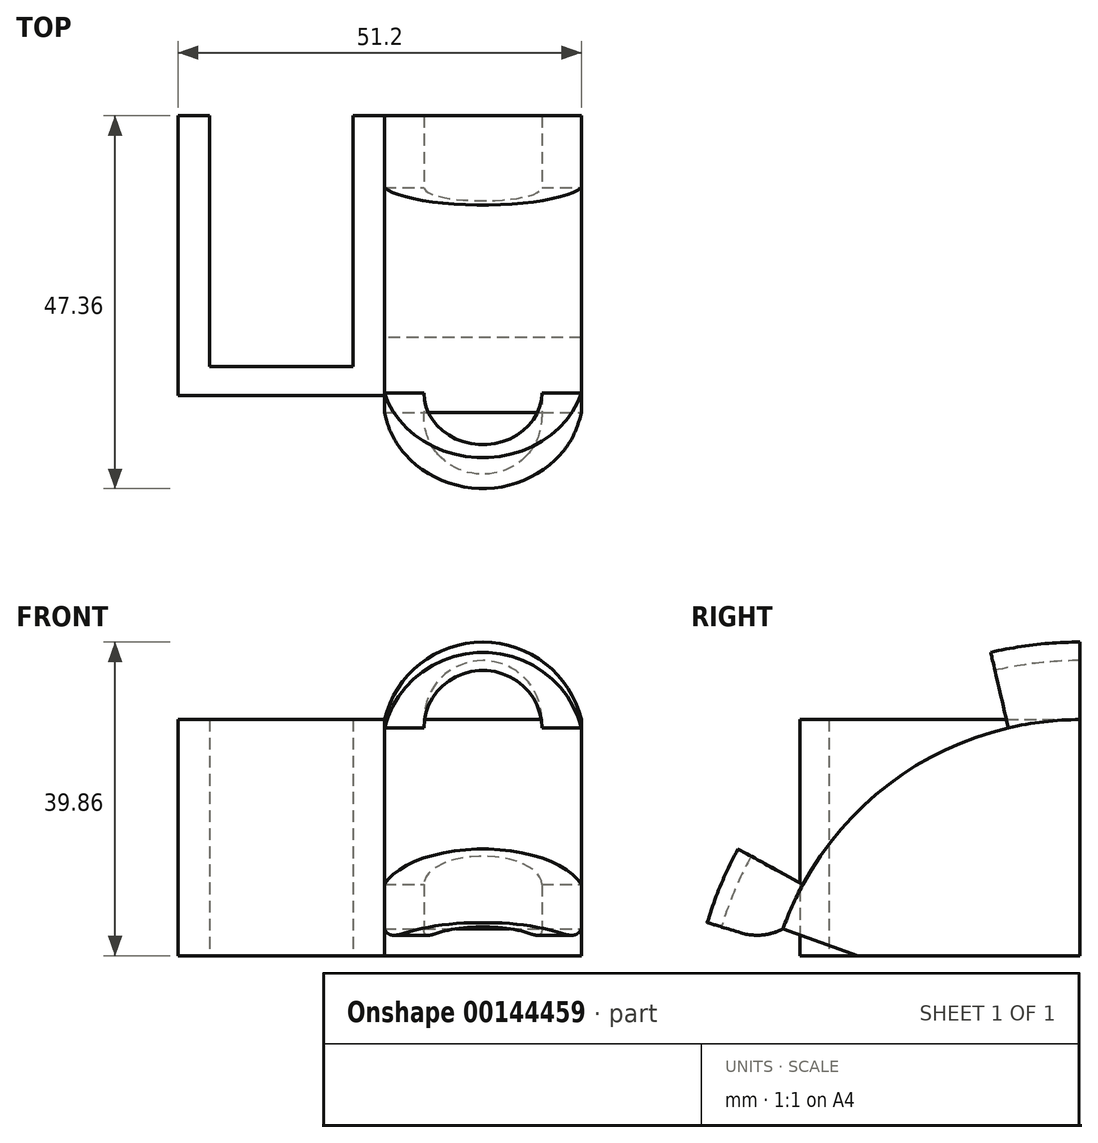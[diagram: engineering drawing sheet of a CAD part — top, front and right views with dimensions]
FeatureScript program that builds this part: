
annotation { "Feature Type Name" : "Feature", "Feature Type Description" : "" }
export const myFeature = defineFeature(function(context is Context, id is Id, definition is map)
    precondition{}
    {
        {
            var Q0;
            Q0=qCreatedBy(makeId("Top.planeOp"),FACE);
            var sketch = newSketch(context, id + "F0", { "sketchPlane" : qUnion([Q0])});
            skLineSegment(sketch, "E0.bottom", {"start": v(0, 0) * mm, "end": v(-4, 0) * mm});
            skLineSegment(sketch, "E0.top", {"start": v(0, 35.56) * mm, "end": v(-4, 35.56) * mm});
            skLineSegment(sketch, "E0.left", {"start": v(0, 0) * mm, "end": v(0, 35.56) * mm});
            skLineSegment(sketch, "E0.right", {"start": v(-4, 0) * mm, "end": v(-4, 35.56) * mm});
            skLineSegment(sketch, "E1.bottom", {"start": v(-4, 0) * mm, "end": v(-22.2, 0) * mm});
            skLineSegment(sketch, "E1.top", {"start": v(-4, 3.67) * mm, "end": v(-22.2, 3.67) * mm});
            skLineSegment(sketch, "E1.left", {"start": v(-4, 0) * mm, "end": v(-4, 3.67) * mm});
            skLineSegment(sketch, "E1.right", {"start": v(-22.2, 0) * mm, "end": v(-22.2, 3.67) * mm});
            skLineSegment(sketch, "E2.bottom", {"start": v(-22.2, 0) * mm, "end": v(-26.2, 0) * mm});
            skLineSegment(sketch, "E2.top", {"start": v(-22.2, 35.56) * mm, "end": v(-26.2, 35.56) * mm});
            skLineSegment(sketch, "E2.left", {"start": v(-22.2, 0) * mm, "end": v(-22.2, 35.56) * mm});
            skLineSegment(sketch, "E2.right", {"start": v(-26.2, 0) * mm, "end": v(-26.2, 35.56) * mm});
            skSolve(sketch);
        }
        {
            var Q0;
            Q0 = qSketchRegion(id + "F0", true);
            extrude(context, id + "F1", {"entities" : qUnion([Q0]), "depth" : 30 * mm});
        }
        {
            var Q0;
            Q0=makeQuery(id+"F1.opExtrude","SWEPT_FACE",FACE,{"disambiguationData":[OSD([sQuery(id+"F0.wireOp",EDGE,"E0.left")])]});
            var sketch = newSketch(context, id + "F2", { "sketchPlane" : qUnion([Q0])});
            skArc(sketch, "E3", {"start": v(35.56, 19.88) * mm, "mid": v(18.32, 14.4) * mm, "end": v(7.36, 0) * mm});
            skLineSegment(sketch, "E4", {"start": v(35.56, 0) * mm, "end": v(7.36, 0) * mm});
            skLineSegment(sketch, "E5", {"start": v(35.56, 0) * mm, "end": v(35.56, 19.88) * mm});
            skLineSegment(sketch, "E6", {"start": v(35.56, 30) * mm, "end": v(35.56, -28.36) * mm, "construction": true});
            skPoint(sketch, "E6.endSnap0", {"position": v(35.56, 9.94) * mm});
            skLineSegment(sketch, "E7", {"start": v(35.6, -10.12) * mm, "end": v(0, -10.12) * mm, "construction": true});
            skSolve(sketch);
        }
        {
            var Q0;
            {var subQ0=sQuery(id+"F2.wireOp",EDGE,"E4");Q0=makeQuery(id+"F2.imprint","IMPRINT",FACE,{"disambiguationData":[TD([[makeQuery(id+"F2.imprint","IMPRINT",EDGE,{"derivedFrom":subQ0}),1.0]])]});}
            extrude(context, id + "F3", {"entities" : qUnion([Q0]), "operationType" : NewBodyOperationType.ADD, "depth" : 25 * mm});
        }
        {
            var Q0;
            Q0=makeQuery(id+"F3.boolean.opBoolean","MERGE",FACE,{"derivedFrom":[makeQuery(id+"F1.opExtrude","SWEPT_FACE",FACE,{"disambiguationData":[OSD([sQuery(id+"F0.wireOp",EDGE,"E0.top")])]}),makeQuery(id+"F3.opExtrude","SWEPT_FACE",FACE,{"disambiguationData":[OSD([sQuery(id+"F2.wireOp",EDGE,"E5")])]})]});
            var sketch = newSketch(context, id + "F4", { "sketchPlane" : qUnion([Q0])});
            skLineSegment(sketch, "E8", {"start": v(0, 30) * mm, "end": v(0, 19.88) * mm});
            skLineSegment(sketch, "E9", {"start": v(0, 19.88) * mm, "end": v(-25, 19.88) * mm});
            skLineSegment(sketch, "E10", {"start": v(-25, 19.88) * mm, "end": v(-25, 30) * mm});
            skLineSegment(sketch, "E11", {"start": v(0, 30) * mm, "end": v(-25, 30) * mm});
            skCircle(sketch, "E12", {"center": v(-12.5, 30) * mm, "radius": 7.5 * mm});
            skSolve(sketch);
        }
        {
            var Q0;
            {var subQ0=sQuery(id+"F4.wireOp",EDGE,"E11");var subQ6=sQuery(id+"F4.wireOp",EDGE,"E12");var subQ7=makeQuery(id+"F4.imprint","INTERSECT",VERTEX,{"disambiguationData":[OD(0.0)],"derivedFrom":[subQ0,subQ6]});Q0=makeQuery(id+"F4.imprint","IMPRINT",FACE,{"disambiguationData":[TD([[makeQuery(id+"F4.imprint","IMPRINT",EDGE,{"disambiguationData":[TD([[subQ7,1.0]])],"derivedFrom":subQ0}),1.0]])]});}
            var Q1;
            {var subQ0=sQuery(id+"F4.wireOp",EDGE,"E10");var subQ3=sQuery(id+"F4.wireOp",EDGE,"E11");var subQ4=makeQuery(id+"F4.imprint","INTERSECT",VERTEX,{"derivedFrom":[subQ0,subQ3]});Q1=makeQuery(id+"F4.imprint","IMPRINT",FACE,{"disambiguationData":[TD([[makeQuery(id+"F4.imprint","IMPRINT",EDGE,{"disambiguationData":[TD([[subQ4,1.0]])],"derivedFrom":subQ3}),1.0]])]});}
            var Q2;
            Q2=sQuery(id+"F2.wireOp",EDGE,"E3");
            sweep(context, id + "F5", {"operationType" : NewBodyOperationType.ADD, "profiles" : qUnion([Q0, Q1]), "path" : qUnion([Q2])});
        }
        {
            var Q0;
            {var subQ0=sQuery(id+"F2.wireOp",EDGE,"E5");var subQ1=sQuery(id+"F0.wireOp",EDGE,"E0.top");Q0=makeQuery(id+"F5.boolean.opBoolean","MERGE",FACE,{"derivedFrom":[makeQuery(id+"F3.boolean.opBoolean","MERGE",FACE,{"derivedFrom":[makeQuery(id+"F1.opExtrude","SWEPT_FACE",FACE,{"disambiguationData":[OSD([subQ1])]}),makeQuery(id+"F3.opExtrude","SWEPT_FACE",FACE,{"disambiguationData":[OSD([subQ0])]})]}),makeQuery(id+"F5.opSweep","CAP_FACE",FACE,{"disambiguationData":[OSD([subQ1,sQuery(id+"F0.wireOp",EDGE,"E0.right"),sQuery(id+"F2.wireOp",VERTEX,"E3.start"),sQuery(id+"F2.wireOp",EDGE,"E4"),subQ0,sQuery(id+"F4.wireOp",EDGE,"E10"),sQuery(id+"F4.wireOp",EDGE,"E11"),sQuery(id+"F4.wireOp",EDGE,"E12")])],"isStart":true})]});}
            var sketch = newSketch(context, id + "F6", { "sketchPlane" : qUnion([Q0])});
            skArc(sketch, "E13", {"start": v(-5, 30) * mm, "mid": v(-12.5, 37.5) * mm, "end": v(-20, 30) * mm});
            skArc(sketch, "E14", {"start": v(0, 30) * mm, "mid": v(-12.5, 39.86) * mm, "end": v(-25, 30) * mm});
            skLineSegment(sketch, "E15", {"start": v(-25, 30) * mm, "end": v(-20, 30) * mm});
            skLineSegment(sketch, "E16", {"start": v(-5, 30) * mm, "end": v(0, 30) * mm});
            skSolve(sketch);
        }
        {
            var Q0;
            {var subQ0=sQuery(id+"F2.wireOp",EDGE,"E3");Q0=makeQuery(id+"F5.boolean.opBoolean","MERGE",FACE,{"derivedFrom":[makeQuery(id+"F3.opExtrude","CAP_FACE",FACE,{"disambiguationData":[OSD([subQ0,sQuery(id+"F2.wireOp",EDGE,"E4"),sQuery(id+"F2.wireOp",EDGE,"E5")])],"isStart":false}),makeQuery(id+"F5.opSweep","SWEPT_FACE",FACE,{"disambiguationData":[OSD([subQ0,sQuery(id+"F4.wireOp",EDGE,"E10")])]})]});}
            var sketch = newSketch(context, id + "F7", { "sketchPlane" : qUnion([Q0])});
            skArc(sketch, "E17", {"start": v(35.56, 24.88) * mm, "mid": v(31.56, 24.64) * mm, "end": v(27.62, 23.95) * mm});
            skLineSegment(sketch, "E18", {"start": v(35.6, -10.12) * mm, "end": v(35.56, 24.88) * mm});
            skLineSegment(sketch, "E19", {"start": v(35.6, -10.12) * mm, "end": v(27.62, 23.95) * mm});
            skSolve(sketch);
        }
        {
            var Q0;
            Q0=makeQuery(id+"F6.imprint","IMPRINT",FACE,{"disambiguationData":[TD([[makeQuery(id+"F6.imprint","IMPRINT",EDGE,{"derivedFrom":sQuery(id+"F6.wireOp",EDGE,"E13")}),-1.0]])]});
            var Q1;
            Q1=sQuery(id+"F7.wireOp",EDGE,"E17");
            sweep(context, id + "F8", {"operationType" : NewBodyOperationType.ADD, "profiles" : qUnion([Q0]), "path" : qUnion([Q1])});
        }
        {
            var Q0;
            Q0=makeQuery(id+"F5.opSweep","CAP_FACE",FACE,{"disambiguationData":[OSD([sQuery(id+"F2.wireOp",VERTEX,"E3.end"),sQuery(id+"F4.wireOp",EDGE,"E8"),sQuery(id+"F4.wireOp",EDGE,"E9"),sQuery(id+"F4.wireOp",EDGE,"E10"),sQuery(id+"F4.wireOp",EDGE,"E11"),sQuery(id+"F4.wireOp",EDGE,"E12")])],"isStart":false});
            var sketch = newSketch(context, id + "F9", { "sketchPlane" : qUnion([Q0])});
            skArc(sketch, "E20", {"start": v(20, 3.2) * mm, "mid": v(12.5, 10.7) * mm, "end": v(5, 3.2) * mm});
            skArc(sketch, "E21", {"start": v(25, 3.2) * mm, "mid": v(12.5, 12.6) * mm, "end": v(0, 3.2) * mm});
            skLineSegment(sketch, "E22", {"start": v(0, 3.2) * mm, "end": v(5, 3.2) * mm});
            skLineSegment(sketch, "E23", {"start": v(20, 3.2) * mm, "end": v(25, 3.2) * mm});
            skSolve(sketch);
        }
        {
            var Q0;
            {var subQ0=sQuery(id+"F2.wireOp",EDGE,"E3");Q0=makeQuery(id+"F5.boolean.opBoolean","MERGE",FACE,{"derivedFrom":[makeQuery(id+"F3.opExtrude","CAP_FACE",FACE,{"disambiguationData":[OSD([subQ0,sQuery(id+"F2.wireOp",EDGE,"E4"),sQuery(id+"F2.wireOp",EDGE,"E5")])],"isStart":false}),makeQuery(id+"F5.opSweep","SWEPT_FACE",FACE,{"disambiguationData":[OSD([subQ0,sQuery(id+"F4.wireOp",EDGE,"E10")])]})]});}
            var sketch = newSketch(context, id + "F10", { "sketchPlane" : qUnion([Q0])});
            skArc(sketch, "E24", {"start": v(4.86, 6.6) * mm, "mid": v(3.3, 3.37) * mm, "end": v(2.1, 0) * mm});
            skLineSegment(sketch, "E25", {"start": v(35.6, -10.12) * mm, "end": v(2.1, 0) * mm});
            skLineSegment(sketch, "E26", {"start": v(35.6, -10.12) * mm, "end": v(4.86, 6.6) * mm});
            skSolve(sketch);
        }
        {
            var Q0;
            Q0=makeQuery(id+"F9.imprint","IMPRINT",FACE,{"disambiguationData":[TD([[makeQuery(id+"F9.imprint","IMPRINT",EDGE,{"derivedFrom":sQuery(id+"F9.wireOp",EDGE,"E20")}),-1.0]])]});
            var Q1;
            Q1=sQuery(id+"F10.wireOp",EDGE,"E24");
            sweep(context, id + "F11", {"operationType" : NewBodyOperationType.ADD, "profiles" : qUnion([Q0]), "path" : qUnion([Q1])});
        }
        {
            var Q0;
            Q0=makeQuery(id+"F8.opSweep","CAP_EDGE",EDGE,{"disambiguationData":[OSD([sQuery(id+"F6.wireOp",EDGE,"E16"),sQuery(id+"F7.wireOp",VERTEX,"E17.end")])],"isStart":false});
            var Q1;
            Q1=makeQuery(id+"F8.opSweep","CAP_EDGE",EDGE,{"disambiguationData":[OSD([sQuery(id+"F6.wireOp",EDGE,"E15"),sQuery(id+"F7.wireOp",VERTEX,"E17.end")])],"isStart":false});
            var Q2;
            Q2=makeQuery(id+"F11.opSweep","CAP_EDGE",EDGE,{"disambiguationData":[OSD([sQuery(id+"F9.wireOp",EDGE,"E23"),sQuery(id+"F10.wireOp",VERTEX,"E24.start")])],"isStart":false});
            var Q3;
            Q3=makeQuery(id+"F11.opSweep","CAP_EDGE",EDGE,{"disambiguationData":[OSD([sQuery(id+"F9.wireOp",EDGE,"E22"),sQuery(id+"F10.wireOp",VERTEX,"E24.start")])],"isStart":false});
            fillet(context, id + "F12", {"entities" : qUnion([Q0, Q1, Q2, Q3]), "radius" : 7 * mm, "tangentPropagation" : true, "allowEdgeOverflow" : false});
        }
    });
